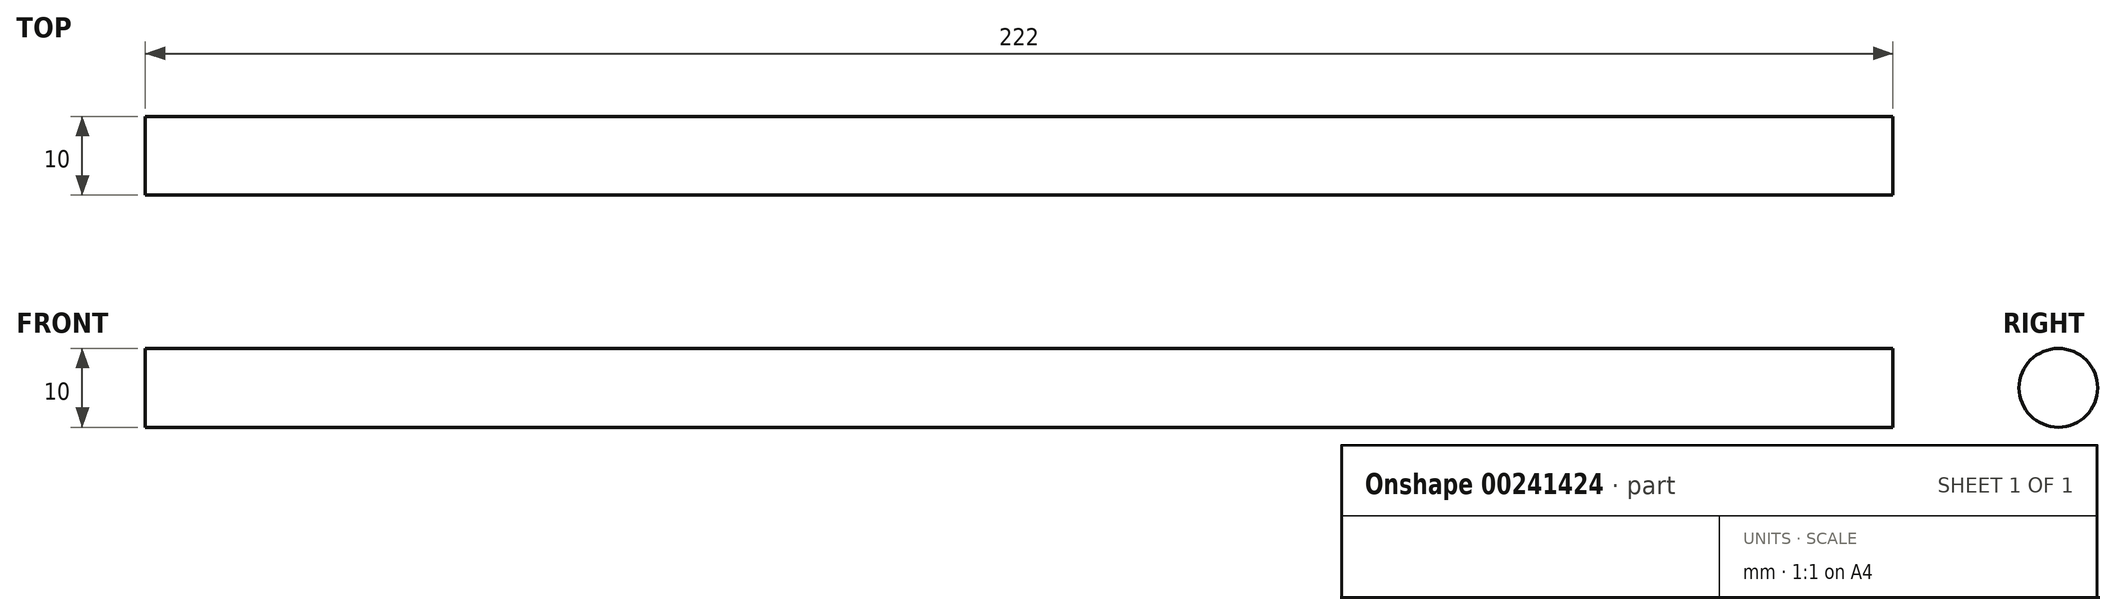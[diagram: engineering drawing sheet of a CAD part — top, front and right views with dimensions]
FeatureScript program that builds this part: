
annotation { "Feature Type Name" : "Feature", "Feature Type Description" : "" }
export const myFeature = defineFeature(function(context is Context, id is Id, definition is map)
    precondition{}
    {
        {
            var Q0;
            Q0=qCreatedBy(makeId("Right.planeOp"),FACE);
            var sketch = newSketch(context, id + "F0", { "sketchPlane" : qUnion([Q0])});
            skCircle(sketch, "E0", {"center": v(0, 0) * mm, "radius": 5 * mm});
            skSolve(sketch);
        }
        {
            var Q0;
            Q0 = qSketchRegion(id + "F0", true);
            extrude(context, id + "F1", {"entities" : qUnion([Q0]), "depth" : 222 * mm});
        }
    });
